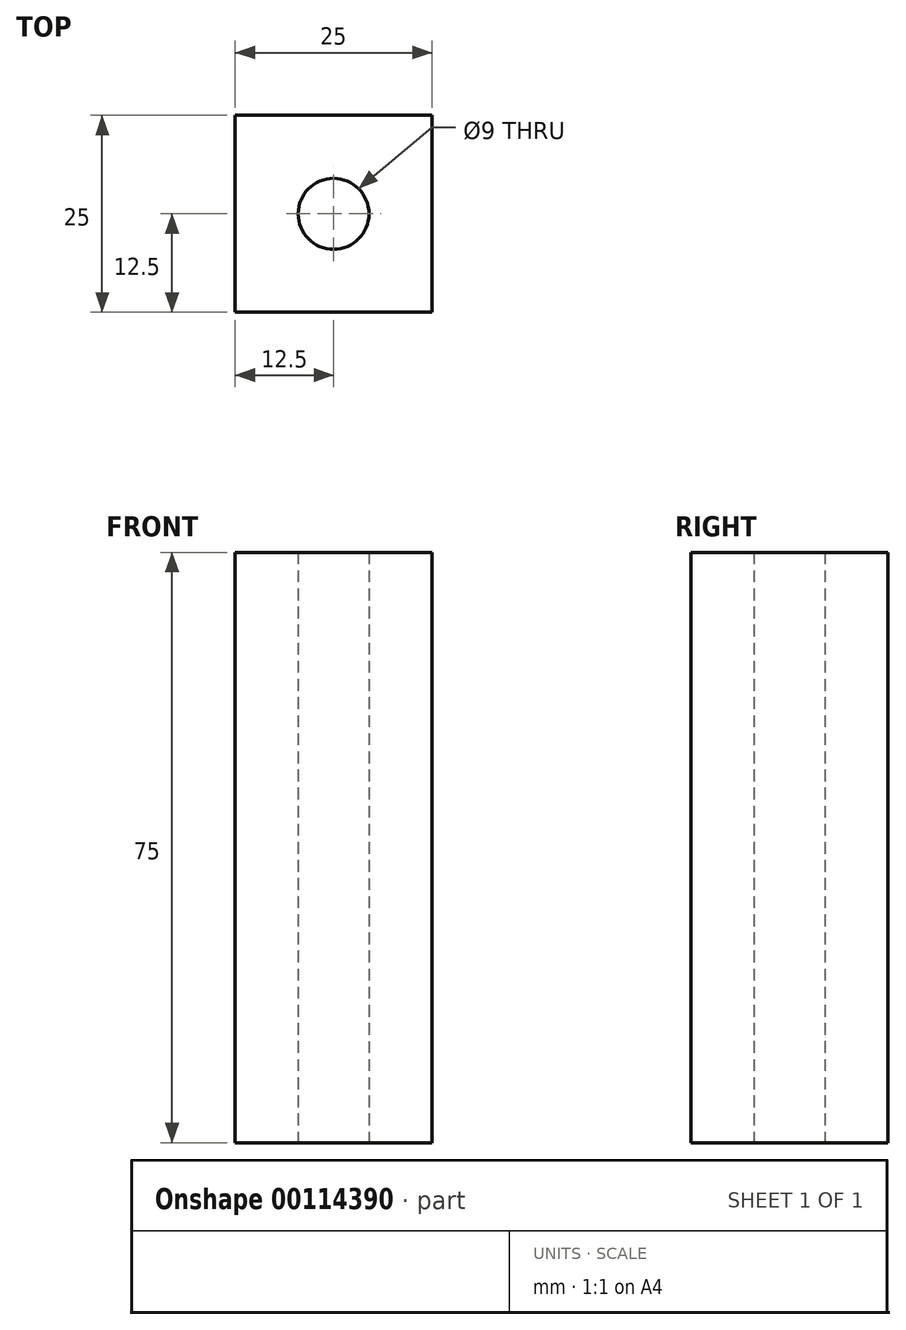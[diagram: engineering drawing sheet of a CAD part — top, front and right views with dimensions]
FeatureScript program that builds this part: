
annotation { "Feature Type Name" : "Feature", "Feature Type Description" : "" }
export const myFeature = defineFeature(function(context is Context, id is Id, definition is map)
    precondition{}
    {
        {
            var Q0;
            Q0=qCreatedBy(makeId("Top.planeOp"),FACE);
            var sketch = newSketch(context, id + "F0", { "sketchPlane" : qUnion([Q0])});
            skLineSegment(sketch, "E0.bottom", {"start": v(12.5, -12.5) * mm, "end": v(-12.5, -12.5) * mm});
            skLineSegment(sketch, "E0.top", {"start": v(12.5, 12.5) * mm, "end": v(-12.5, 12.5) * mm});
            skLineSegment(sketch, "E0.left", {"start": v(12.5, -12.5) * mm, "end": v(12.5, 12.5) * mm});
            skLineSegment(sketch, "E0.right", {"start": v(-12.5, -12.5) * mm, "end": v(-12.5, 12.5) * mm});
            skPoint(sketch, "E0.middle", {"position": v(0, 0) * mm});
            skCircle(sketch, "E1", {"center": v(0, 0) * mm, "radius": 4.5 * mm});
            skSolve(sketch);
        }
        {
            var Q0;
            Q0 = qSketchRegion(id + "F0", true);
            extrude(context, id + "F1", {"entities" : qUnion([Q0]), "depth" : 75 * mm});
        }
    });
